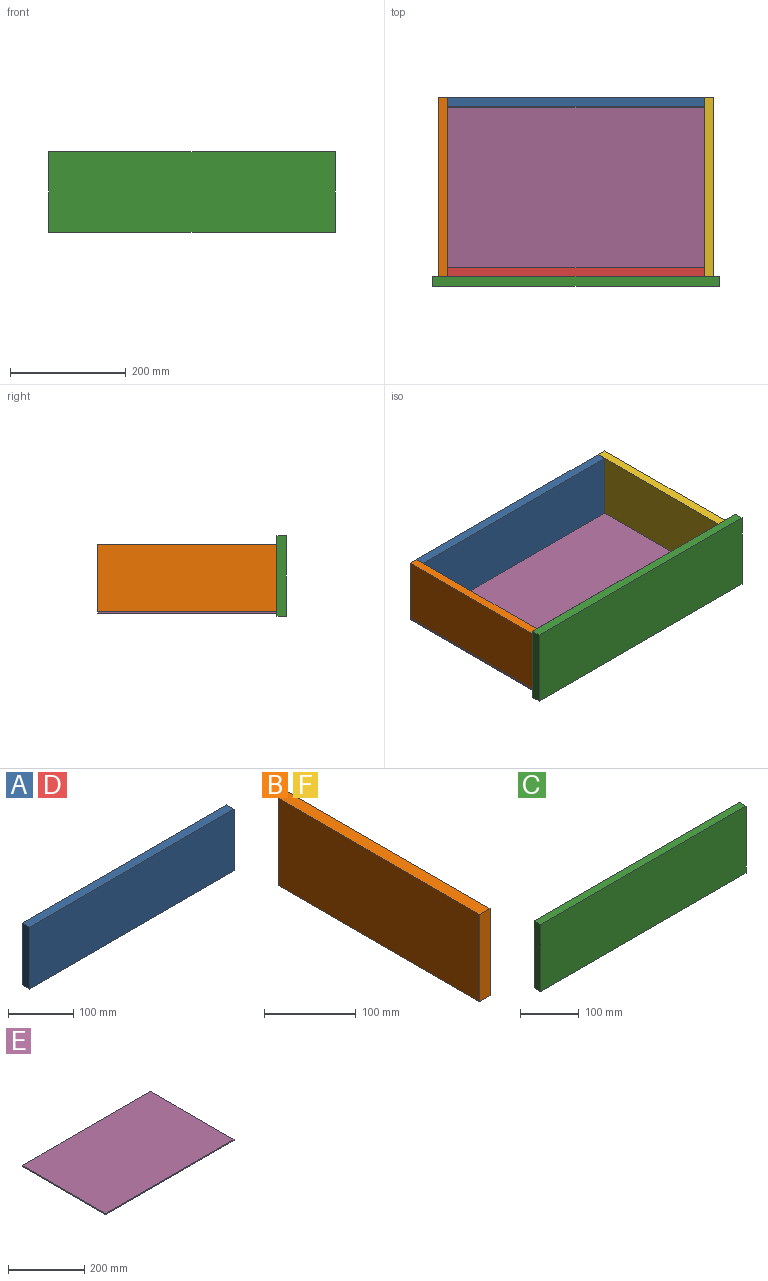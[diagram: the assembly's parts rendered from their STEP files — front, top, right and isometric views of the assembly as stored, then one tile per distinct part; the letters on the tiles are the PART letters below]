
ASSEMBLY  parts=6 mates=6
PART A: 6 faces, bbox 444x16x116 mm
  f0: plane 444x16mm, normal (0,0,-1), area 7104mm2, adj f1,f3,f4,f5
  f1: plane 116x16mm, normal (-1,0,0), area 1856mm2, adj f0,f2,f4,f5
  f2: plane 444x16mm, normal (0,0,1), area 7104mm2, adj f1,f3,f4,f5
  f3: plane 116x16mm, normal (1,0,0), area 1856mm2, adj f0,f2,f4,f5
  f4: plane 444x116mm, normal (0,1,0), area 51504mm2, adj f0,f1,f2,f3
  f5: plane 444x116mm, normal (0,-1,0), area 51504mm2, adj f0,f1,f2,f3
PART B: 6 faces, bbox 16x310x116 mm
  f0: plane 310x116mm, normal (1,0,0), area 35960mm2, adj f1,f3,f4,f5
  f1: plane 310x16mm, normal (0,0,-1), area 4960mm2, adj f0,f2,f4,f5
  f2: plane 310x116mm, normal (-1,0,0), area 35960mm2, adj f1,f3,f4,f5
  f3: plane 310x16mm, normal (0,0,1), area 4960mm2, adj f0,f2,f4,f5
  f4: plane 116x16mm, normal (0,1,0), area 1856mm2, adj f0,f1,f2,f3
  f5: plane 116x16mm, normal (0,-1,0), area 1856mm2, adj f0,f1,f2,f3
PART C: 6 faces, bbox 496x16x140 mm
  f0: plane 140x16mm, normal (-1,0,0), area 2240mm2, adj f1,f3,f4,f5
  f1: plane 496x16mm, normal (0,0,-1), area 7936mm2, adj f0,f2,f4,f5
  f2: plane 140x16mm, normal (1,0,0), area 2240mm2, adj f1,f3,f4,f5
  f3: plane 496x16mm, normal (0,0,1), area 7936mm2, adj f0,f2,f4,f5
  f4: plane 496x140mm, normal (0,1,0), area 69440mm2, adj f0,f1,f2,f3
  f5: plane 496x140mm, normal (0,-1,0), area 69440mm2, adj f0,f1,f2,f3
PART D: same geometry as A
PART E: 6 faces, bbox 476x310x3.2 mm
  f0: plane 476x3.2mm, normal (0,1,0), area 1523.2mm2, adj f1,f3,f4,f5
  f1: plane 310x3.2mm, normal (1,0,0), area 992mm2, adj f0,f2,f4,f5
  f2: plane 476x3.2mm, normal (0,-1,0), area 1523.2mm2, adj f1,f3,f4,f5
  f3: plane 310x3.2mm, normal (-1,0,0), area 992mm2, adj f0,f2,f4,f5
  f4: plane 476x310mm, normal (0,0,-1), area 147560mm2, adj f0,f1,f2,f3
  f5: plane 476x310mm, normal (0,0,1), area 147560mm2, adj f0,f1,f2,f3
PART F: same geometry as B
PLACE A t=(0,294,0)mm
PLACE B t=(-460,0,0)mm
PLACE C at identity fixed
PLACE D at identity fixed
PLACE E at identity fixed
PLACE F at identity fixed
MATE planar A.f1 <-> B.f0  axis (-1,0,0) through (-740,139.5,-378.8)mm
MATE planar E.f5 <-> A.f0  axis (0,0,1) through (-518,-7.5,-436.8)mm
MATE planar C.f4 <-> B.f5  axis (0,1,0) through (-766,-162.5,-375)mm
MATE planar B.f1 <-> E.f5  axis (0,0,-1) through (-748,-7.5,-436.8)mm
MATE planar B.f2 <-> E.f3  axis (-1,0,0) through (-756,-7.5,-378.8)mm
MATE planar A.f4 <-> F.f4  axis (0,1,0) through (-518,147.5,-378.8)mm
